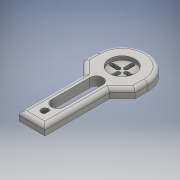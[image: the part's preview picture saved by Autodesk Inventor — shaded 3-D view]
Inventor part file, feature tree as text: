
AUTODESK INVENTOR PART (.ipt)
format: ipt  version: 2016 (Build 200138000, 138)  size: 210,432 bytes
history: native  units: mm
features: extrude x5, sketch x5, fillet x2, other x1, chamfer x1
ambient origin geometry x8: Origin, YZ Plane, XZ Plane, XY Plane, X Axis, Y Axis, Z Axis, Center Point
bodies: Body1 (feature_tree)
feature tree (14):
  other  "LowerArm"
  extrude  "Extrusion11"  Depth=20.0mm
  extrude  "Extrusion12"  Depth=20.0mm
  extrude  "Extrusion13"  Depth=10.0mm
  extrude  "Extrusion14"  Depth=7.0mm TaperAngle=0.0deg
  fillet  "Fillet13"  Radius=20.0mm
  chamfer  "Chamfer1"  Distance=3.0mm
  extrude  "Extrusion15"  Depth=10.0mm
  fillet  "Fillet14"  Radius=1.905mm
  sketch  "Sketch1"  dims[d0=50.0mm d2=20.0mm]
  sketch  "Sketch11"  dims[d84=40.0mm d85=20.0mm]
  sketch  "Sketch12"  dims[d86=20.0mm d87=10.0mm]
  sketch  "Sketch13"  dims[d88=50.0mm d89=7.0mm d90=0.0mm d91=20.0mm d92=3.0mm d93=0.0mm]
  sketch  "Sketch14"  dims[d94=5.58mm d95=10.0mm d96=1.905mm d97=10.0mm d98=0.0mm d99=1.5mm d100=8.0mm d101=1.5mm d102=30.0mm d103=8.0mm d104=1.5mm d105=11.499983mm d106=40.0mm d108=360.0deg d110=10.0mm d111=0.0mm d112=20.0mm d113=10.0mm d114=2.0mm d115=45.0deg d116=20.0mm d117=30.0mm d118=5.0mm d119=5.0mm d120=10.0mm d121=0.0mm d122=3.0mm]
